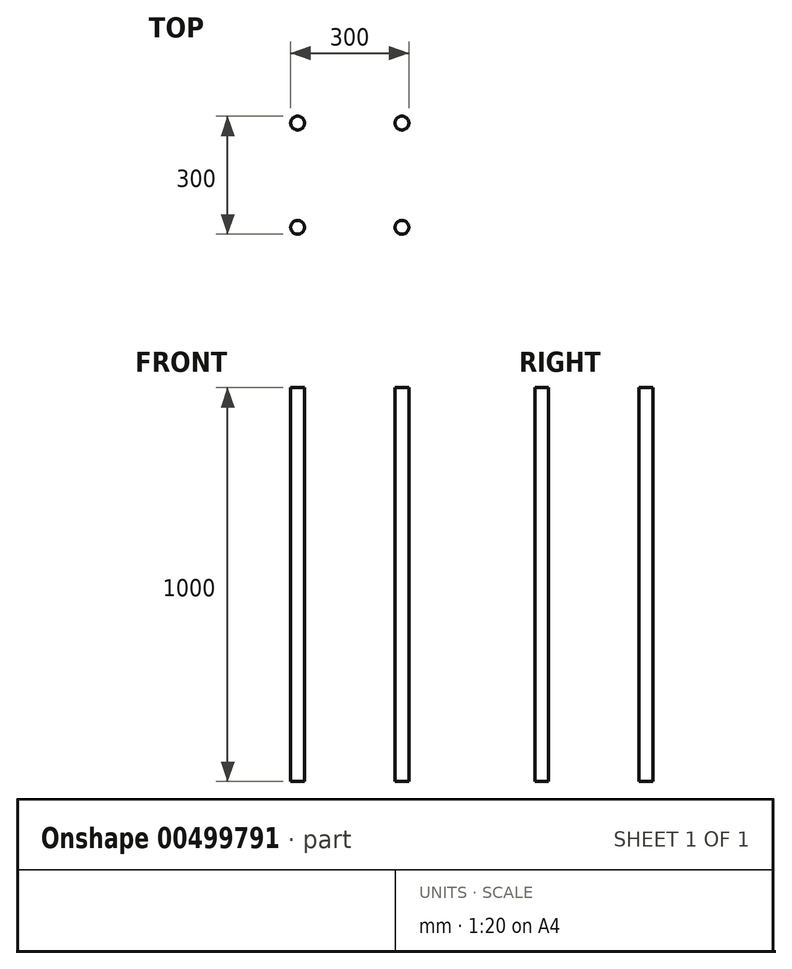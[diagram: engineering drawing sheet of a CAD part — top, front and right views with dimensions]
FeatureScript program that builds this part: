
annotation { "Feature Type Name" : "Feature", "Feature Type Description" : "" }
export const myFeature = defineFeature(function(context is Context, id is Id, definition is map)
    precondition{}
    {
        {
            var Q0;
            Q0=qCreatedBy(makeId("Top.planeOp"),FACE);
            var sketch = newSketch(context, id + "F0", { "sketchPlane" : qUnion([Q0])});
            skCircle(sketch, "E0", {"center": v(-132.5, 132.5) * mm, "radius": 17.5 * mm});
            skCircle(sketch, "E1", {"center": v(132.5, 132.5) * mm, "radius": 17.5 * mm});
            skCircle(sketch, "E2", {"center": v(-132.5, -132.5) * mm, "radius": 17.5 * mm});
            skCircle(sketch, "E3", {"center": v(132.5, -132.5) * mm, "radius": 17.5 * mm});
            skSolve(sketch);
        }
        {
            var Q0;
            Q0 = qSketchRegion(id + "F0", true);
            extrude(context, id + "F1", {"entities" : qUnion([Q0]), "depth" : 1000 * mm});
        }
    });
